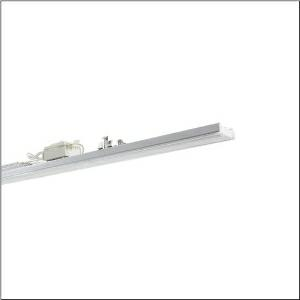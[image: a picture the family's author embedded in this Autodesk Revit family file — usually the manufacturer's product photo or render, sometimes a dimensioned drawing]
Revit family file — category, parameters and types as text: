
# Revit family: licross_r__21_recessed_mo_52te1edv4e5g_90af
name_source: partatom
category: Lighting Fixtures
units: mm (PartAtom-declared; Revit-internal decimal feet)

## family parameters
Cut with Voids When Loaded = No
Host = Face
Light Source = No
Part Type = Normal
Room Calculation Point = No
Round Connector Dimension = Use Diameter
Shared = No

## types (1)
- --- (1 x LED, 14910 lm, 85.3 W, 4000K)
    Apparent Load = 85 VA
    CIE Flux Codes = 85 95 99 100 100
    Color Rendering = 80
    Color Temperature = 4000K
    Default Elevation = 1800 mm
    Description = Licross® 21 Recessed MO, luminaire insert, of sheet steel, galvanised, coil coated, white, length: 2.250mm, width: 66mm, height: 67mm, LED rated luminous flux: 14.910lm, light colour: 840, control gear: DALI 2, with plug, 5-pole, with phase selection, mains connection: 220..240V, AC, 50/60Hz, rated input power: 85W, halogen-free wiring, primary light control with lens, of plastic, primary optical cover: cover, of PMMA, light emission: direct distribution, primary light characteristic: symmetric, protection rating (complete): IP54, insulation class (complete): insulation class I (protective earthing), certification: CE, ENEC, VDE, UKCA, protection symbol: D if used in an environment with non-conductive dust loads with corresponding accessories, impact resistance: IK06, permissible ambient temperature for indoor applications: -25..+35°C, corresponds to IFS (International Featured Standards) requirements for safety and quality in the food industry, reducing of maximum allowable ambient temperature of 5°C with ceiling mounting, LABS conformity tested according to VDMA 24364:2018-05, packaging unit: 1 piece
    Height = 58 mm
    Lamp = 1 x LED
    Lamp Light Flux = 14910 lm
    Lamp Power = 85.3 W
    Lamp count = 1
    Length = 2250 mm
    Luminous efficacy = 175 lm/W
    Manufacturer = Siteco
    ModVariant = No
    Model = 52TE1EDV4E5G
    Mounting Place = Ceiling
    Mounting Type = Pendant
    Number of Poles = 1
    OnlyDefault = Yes
    Power Factor = 1
    Product Name = Licross® 21 Recessed MO
    Product group = luminaire insert
    ProductGroupID = 902
    Protection Class = Protection class I
    Protection Degree = IP 54
    RLX_Detail_Level = 1
    RLX_Emergency_Light_Flux = 0 lm
    RLX_Emergency_Type = 0
    RLX_Emergency_Type_DB = No
    RlxData = <blob elided: 29373 chars, md5=6130b4fc>
    Socket = socket
    Standby Power = 0 W
    System Light Flux = 14910 lm
    System Power = 85 W
    Type Comments = factory setting: luminous flux: 100 % | dim-lin: 254 | 390 mA
    Type Image = l_1296930.jpg
    URL = http://relux.com
    VarID = @adj_125506
    Voltage = 0 V
    Weight = 0.00 kg
    Width = 66 mm

## geometry (parser evidence)
native form markers: Blend x4, Sweep x10
no freeform markers — native parametric forms only
